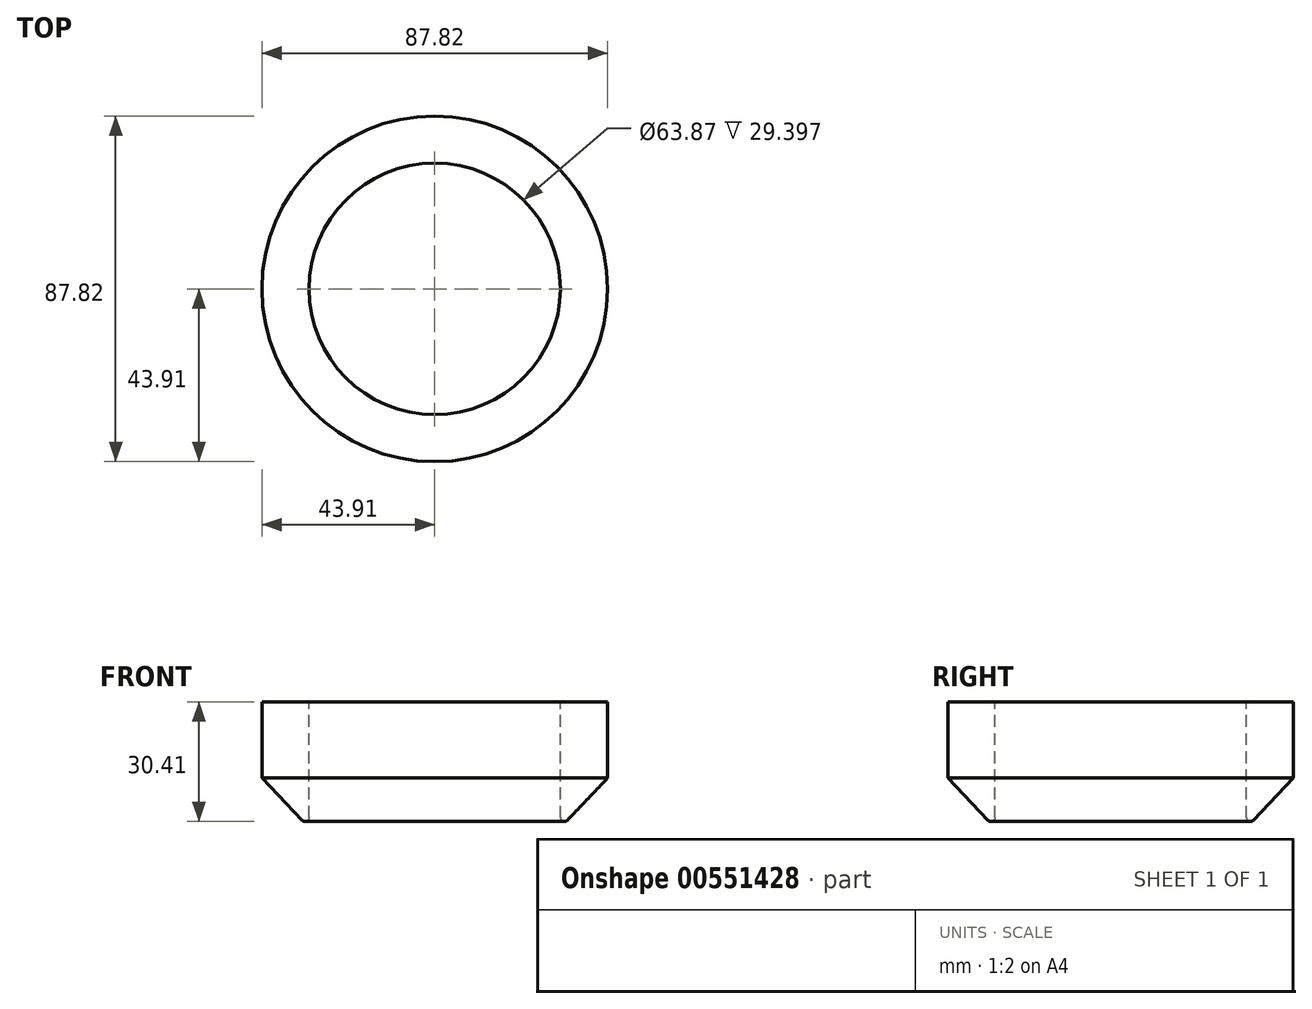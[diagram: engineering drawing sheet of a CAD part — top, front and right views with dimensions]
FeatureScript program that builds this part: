
annotation { "Feature Type Name" : "Feature", "Feature Type Description" : "" }
export const myFeature = defineFeature(function(context is Context, id is Id, definition is map)
    precondition{}
    {
        {
            var Q0;
            Q0=qCreatedBy(makeId("Front.planeOp"),FACE);
            var sketch = newSketch(context, id + "F0", { "sketchPlane" : qUnion([Q0])});
            skLineSegment(sketch, "E0", {"start": v(-31.94, 10.81) * mm, "end": v(-31.94, -18.59) * mm});
            skLineSegment(sketch, "E1", {"start": v(-33.69, -19.29) * mm, "end": v(-43.91, -8.55) * mm});
            skLineSegment(sketch, "E2", {"start": v(-43.91, -8.55) * mm, "end": v(-43.91, 10.81) * mm});
            skLineSegment(sketch, "E3", {"start": v(-31.94, 10.81) * mm, "end": v(-43.91, 10.81) * mm});
            skLineSegment(sketch, "E4", {"start": v(0, 39.76) * mm, "end": v(0, -68.03) * mm, "construction": true});
            skPoint(sketch, "E5.visualSharp", {"position": v(-31.94, -21.13) * mm});
            skArc(sketch, "E5.filletArc", {"start": v(-33.69, -19.29) * mm, "mid": v(-32.58, -19.53) * mm, "end": v(-31.94, -18.59) * mm});
            skSolve(sketch);
        }
        {
            var Q0;
            Q0=makeQuery(id+"F0.imprint","IMPRINT",FACE,{"disambiguationData":[TD([[makeQuery(id+"F0.imprint","IMPRINT",EDGE,{"derivedFrom":sQuery(id+"F0.wireOp",EDGE,"E0")}),-1.0]])]});
            var Q1;
            Q1=sQuery(id+"F0.wireOp",EDGE,"E4");
            revolve(context, id + "F1", {"entities" : qUnion([Q0]), "axis" : qUnion([Q1]), "revolveType" : RevolveType.FULL});
        }
    });
